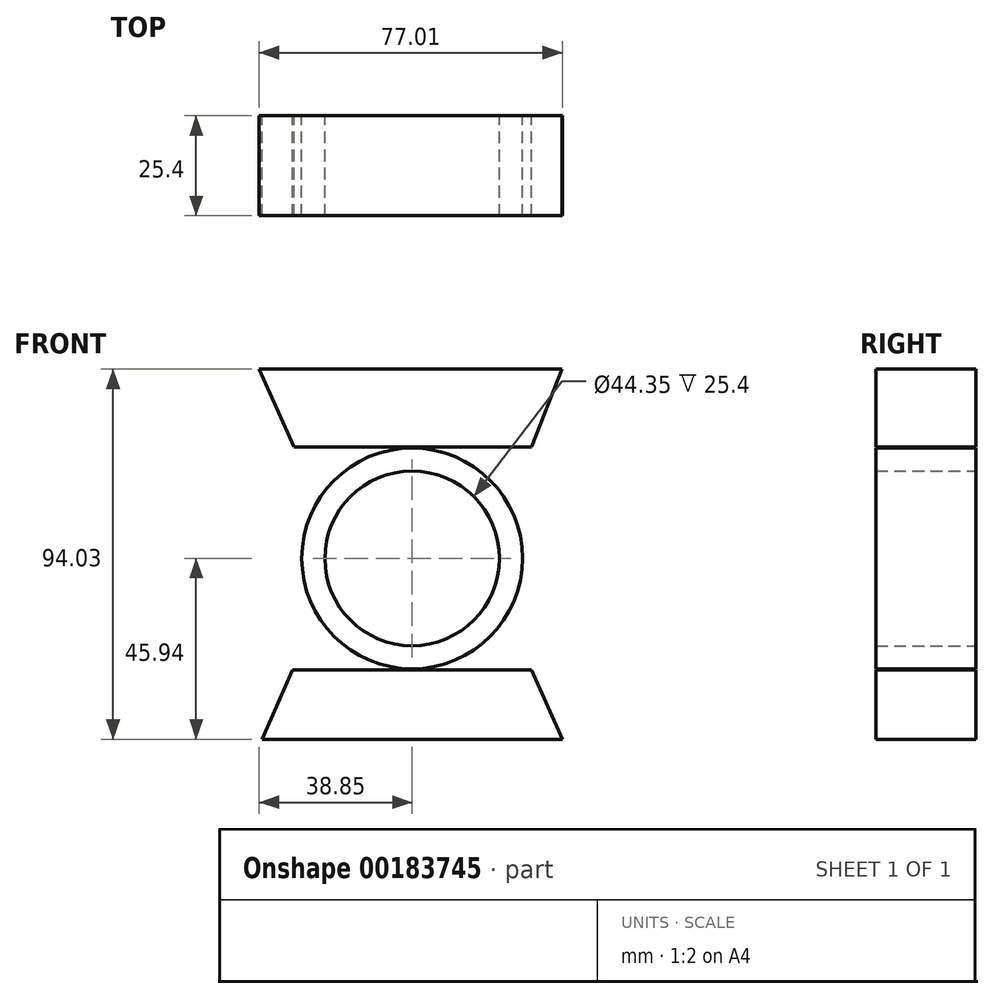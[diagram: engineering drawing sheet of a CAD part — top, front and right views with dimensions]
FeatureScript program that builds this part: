
annotation { "Feature Type Name" : "Feature", "Feature Type Description" : "" }
export const myFeature = defineFeature(function(context is Context, id is Id, definition is map)
    precondition{}
    {
        {
            var Q0;
            Q0=qCreatedBy(makeId("Front.planeOp"),FACE);
            var sketch = newSketch(context, id + "F0", { "sketchPlane" : qUnion([Q0])});
            skLineSegment(sketch, "E0.bottom", {"start": v(30.3, -28.32) * mm, "end": v(-30.43, -28.32) * mm});
            skLineSegment(sketch, "E0.top", {"start": v(38.16, -45.94) * mm, "end": v(-38.16, -45.94) * mm});
            skLineSegment(sketch, "E1", {"start": v(-38.16, -45.94) * mm, "end": v(-30.43, -28.32) * mm});
            skLineSegment(sketch, "E2", {"start": v(38.16, -45.94) * mm, "end": v(30.3, -28.32) * mm});
            skCircle(sketch, "E3", {"center": v(0, 0) * mm, "radius": 28.04 * mm});
            skCircle(sketch, "E4", {"center": v(0, 0) * mm, "radius": 22.18 * mm});
            skLineSegment(sketch, "E5.bottom", {"start": v(-30.03, 28.35) * mm, "end": v(30.3, 28.35) * mm});
            skLineSegment(sketch, "E5.top", {"start": v(-30.03, 48.09) * mm, "end": v(34.23, 48.09) * mm});
            skLineSegment(sketch, "E6.top", {"start": v(-35.07, 48.09) * mm, "end": v(38, 48.09) * mm});
            skLineSegment(sketch, "E7", {"start": v(30.3, 28.35) * mm, "end": v(38, 48.09) * mm});
            skLineSegment(sketch, "E8.top", {"start": v(-38.85, 48.09) * mm, "end": v(38, 48.09) * mm});
            skLineSegment(sketch, "E9", {"start": v(-30.03, 28.35) * mm, "end": v(-38.85, 48.09) * mm});
            skPoint(sketch, "E10.orphan", {"position": v(-38.85, 28.35) * mm});
            skPoint(sketch, "E11.orphan", {"position": v(-35.07, 28.35) * mm});
            skSolve(sketch);
        }
        {
            var Q0;
            Q0 = qSketchRegion(id + "F0", true);
            extrude(context, id + "F1", {"entities" : qUnion([Q0]), "depth" : 25.4 * mm});
        }
    });
